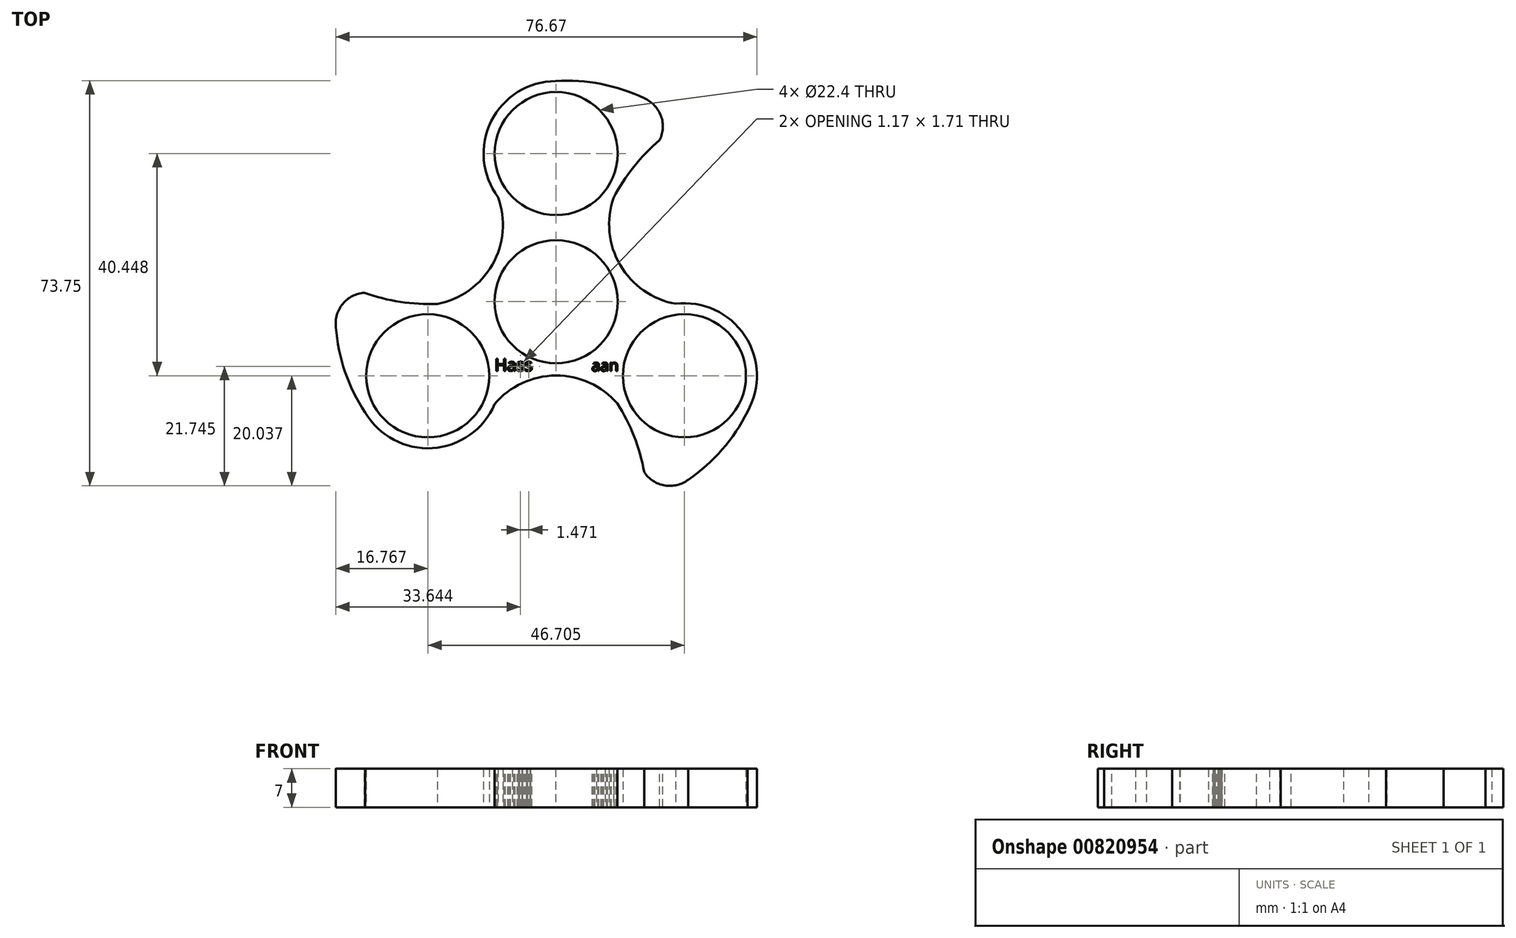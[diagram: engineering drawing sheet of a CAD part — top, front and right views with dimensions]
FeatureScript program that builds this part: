
annotation { "Feature Type Name" : "Feature", "Feature Type Description" : "" }
export const myFeature = defineFeature(function(context is Context, id is Id, definition is map)
    precondition{}
    {
        {
            var Q0;
            Q0=qCreatedBy(makeId("Top.planeOp"),FACE);
            var sketch = newSketch(context, id + "F0", { "sketchPlane" : qUnion([Q0])});
            skCircle(sketch, "E0", {"center": v(0, 0) * mm, "radius": 11.2 * mm});
            skArc(sketch, "E1", {"start": v(10.47, 18.92) * mm, "mid": v(11.4, 20.3) * mm, "end": v(12.14, 21.78) * mm});
            skCircle(sketch, "E2", {"center": v(0, 26.97) * mm, "radius": 11.2 * mm});
            skArc(sketch, "E3.1.0", {"start": v(-21.62, -0.4) * mm, "mid": v(-23.28, -0.28) * mm, "end": v(-24.93, -0.38) * mm});
            skCircle(sketch, "E3.1.1", {"center": v(-23.35, -13.48) * mm, "radius": 11.2 * mm});
            skArc(sketch, "E3.2.0", {"start": v(11.15, -18.52) * mm, "mid": v(11.88, -20.02) * mm, "end": v(12.8, -21.4) * mm});
            skCircle(sketch, "E3.2.1", {"center": v(23.35, -13.48) * mm, "radius": 11.2 * mm});
            skArc(sketch, "E4", {"start": v(10.47, 18.92) * mm, "mid": v(11.66, 6.67) * mm, "end": v(21.76, -0.38) * mm});
            skArc(sketch, "E5.1.0", {"start": v(-21.62, -0.4) * mm, "mid": v(-11.6, 6.77) * mm, "end": v(-10.55, 19.03) * mm});
            skArc(sketch, "E5.2.0", {"start": v(11.15, -18.52) * mm, "mid": v(-0.06, -13.43) * mm, "end": v(-11.2, -18.66) * mm});
            skArc(sketch, "E6", {"start": v(23.05, 32.47) * mm, "mid": v(12.24, 38.57) * mm, "end": v(-0.07, 40.17) * mm});
            skPoint(sketch, "E6.endSnap0", {"position": v(0.07, 40.17) * mm});
            skArc(sketch, "E7", {"start": v(23.05, 32.47) * mm, "mid": v(15.85, 26.54) * mm, "end": v(10.47, 18.92) * mm});
            skArc(sketch, "E8.1.0", {"start": v(-39.64, 3.72) * mm, "mid": v(-39.52, -8.69) * mm, "end": v(-34.75, -20.14) * mm});
            skArc(sketch, "E8.1.1", {"start": v(-39.64, 3.72) * mm, "mid": v(-30.9, 0.46) * mm, "end": v(-21.62, -0.4) * mm});
            skArc(sketch, "E8.2.0", {"start": v(16.6, -36.2) * mm, "mid": v(27.28, -29.88) * mm, "end": v(34.82, -20.02) * mm});
            skArc(sketch, "E8.2.1", {"start": v(16.6, -36.2) * mm, "mid": v(15.06, -27) * mm, "end": v(11.15, -18.52) * mm});
            skArc(sketch, "E9.trimOffspring", {"start": v(0.07, 40.17) * mm, "mid": v(-11.8, 32.9) * mm, "end": v(-10.55, 19.03) * mm});
            skArc(sketch, "E10.trimOffspring", {"start": v(-34.75, -20.14) * mm, "mid": v(-22.52, -26.66) * mm, "end": v(-11.2, -18.66) * mm});
            skArc(sketch, "E11.trimOffspring", {"start": v(34.82, -20.02) * mm, "mid": v(34.34, -6.17) * mm, "end": v(21.76, -0.38) * mm});
            skSolve(sketch);
        }
        {
            var Q0;
            Q0=makeQuery(id+"F0.imprint","IMPRINT",FACE,{"disambiguationData":[TD([[makeQuery(id+"F0.imprint","IMPRINT",EDGE,{"derivedFrom":sQuery(id+"F0.wireOp",EDGE,"E0")}),-1.0]])]});
            extrude(context, id + "F1", {"entities" : qUnion([Q0]), "depth" : 7 * mm, "offsetDistance" : 25 * mm});
        }
        {
            var Q0;
            Q0=makeQuery(id+"F1.opExtrude","CAP_FACE",FACE,{"disambiguationData":[OSD([sQuery(id+"F0.wireOp",EDGE,"E0"),sQuery(id+"F0.wireOp",EDGE,"E1"),sQuery(id+"F0.wireOp",EDGE,"E2"),sQuery(id+"F0.wireOp",EDGE,"E3.1.0"),sQuery(id+"F0.wireOp",EDGE,"E3.1.1"),sQuery(id+"F0.wireOp",EDGE,"E3.2.0"),sQuery(id+"F0.wireOp",EDGE,"E3.2.1"),sQuery(id+"F0.wireOp",EDGE,"E4"),sQuery(id+"F0.wireOp",EDGE,"E5.1.0"),sQuery(id+"F0.wireOp",EDGE,"E5.2.0")])],"isStart":false});
            var sketch = newSketch(context, id + "F2", { "sketchPlane" : qUnion([Q0])});
            skText(sketch, "E12", { "text": "Hass", "fontName": "OpenSans-Regular.ttf"});
            const initialGuessF2  = {"E12": [-0.01121, -0.0126, 1, 0, 0.00222]};
            skSetInitialGuess(sketch, initialGuessF2);
            skSolve(sketch);
        }
        {
            var Q0;
            Q0=qSketchRegion(id+"F2",true);
            extrude(context, id + "F3", {"entities" : qUnion([Q0]), "operationType" : NewBodyOperationType.REMOVE, "oppositeDirection" : true, "depth" : 13.4 * mm, "offsetDistance" : 25 * mm});
        }
        {
            var Q0;
            {var subQ0=sQuery(id+"F0.wireOp",EDGE,"E5.1.0");var subQ1=sQuery(id+"F0.wireOp",EDGE,"E4");var subQ2=sQuery(id+"F0.wireOp",EDGE,"E3.2.1");var subQ3=sQuery(id+"F0.wireOp",EDGE,"E3.2.0");var subQ4=sQuery(id+"F0.wireOp",EDGE,"E3.1.1");var subQ5=sQuery(id+"F0.wireOp",EDGE,"E5.2.0");var subQ6=sQuery(id+"F0.wireOp",EDGE,"E0");var subQ7=sQuery(id+"F0.wireOp",EDGE,"E3.1.0");var subQ8=sQuery(id+"F0.wireOp",EDGE,"E1");var subQ9=sQuery(id+"F0.wireOp",EDGE,"E2");Q0=makeQuery(id+"F3.boolean.opBoolean","SPLIT",FACE,{"disambiguationData":[TD([makeQuery(id+"F1.opExtrude","SWEPT_FACE",FACE,{"disambiguationData":[OSD([subQ6])]})])],"derivedFrom":makeQuery(id+"F1.opExtrude","CAP_FACE",FACE,{"disambiguationData":[OSD([subQ6,subQ8,subQ9,subQ7,subQ4,subQ3,subQ2,subQ1,subQ0,subQ5])],"isStart":false})});}
            var sketch = newSketch(context, id + "F4", { "sketchPlane" : qUnion([Q0])});
            skText(sketch, "E13", { "text": "aan", "fontName": "OpenSans-Regular.ttf"});
            const initialGuessF4  = {"E13": [0.00646, -0.01262, 1, 0, 0.00205]};
            skSetInitialGuess(sketch, initialGuessF4);
            skSolve(sketch);
        }
        {
            var Q0;
            Q0=qSketchRegion(id+"F4",true);
            extrude(context, id + "F5", {"entities" : qUnion([Q0]), "operationType" : NewBodyOperationType.REMOVE, "oppositeDirection" : true, "depth" : 9.9 * mm, "offsetDistance" : 25 * mm});
        }
        {
            var Q0;
            {var subQ43=sQuery(id+"F0.wireOp",EDGE,"E5.2.0");var subQ47=sQuery(id+"F0.wireOp",EDGE,"E5.1.0");var subQ51=sQuery(id+"F0.wireOp",EDGE,"E4");var subQ55=sQuery(id+"F0.wireOp",EDGE,"E3.2.1");var subQ59=sQuery(id+"F0.wireOp",EDGE,"E3.1.1");var subQ62=sQuery(id+"F0.wireOp",EDGE,"E2");var subQ66=sQuery(id+"F0.wireOp",EDGE,"E1");var subQ70=sQuery(id+"F0.wireOp",EDGE,"E3.1.0");var subQ75=sQuery(id+"F0.wireOp",EDGE,"E0");var subQ76=makeQuery(id+"F1.opExtrude","SWEPT_FACE",FACE,{"disambiguationData":[OSD([subQ75])]});var subQ79=sQuery(id+"F0.wireOp",EDGE,"E3.2.0");Q0=makeQuery(id+"F5.boolean.opBoolean","SPLIT",FACE,{"disambiguationData":[TD([subQ76])],"derivedFrom":makeQuery(id+"F3.boolean.opBoolean","SPLIT",FACE,{"disambiguationData":[TD([subQ76])],"derivedFrom":makeQuery(id+"F1.opExtrude","CAP_FACE",FACE,{"disambiguationData":[OSD([subQ75,subQ66,subQ62,subQ70,subQ59,subQ79,subQ55,subQ51,subQ47,subQ43])],"isStart":false})})});}
            var sketch = newSketch(context, id + "F6", { "sketchPlane" : qUnion([Q0])});
            skSolve(sketch);
        }
        {
            var Q0;
            Q0=makeQuery(id+"F6.imprint","IMPRINT",FACE,{"disambiguationData":[TD([[makeQuery(id+"F6.imprint","IMPRINT",EDGE,{"derivedFrom":makeQuery(id+"F1.opExtrude","CAP_EDGE",EDGE,{"disambiguationData":[OSD([sQuery(id+"F0.wireOp",EDGE,"E0")])],"isStart":false})}),-1.0]])]});
            var sketch = newSketch(context, id + "F7", { "sketchPlane" : qUnion([Q0])});
            skArc(sketch, "E14", {"start": v(-34.8, 1.62) * mm, "mid": v(-38.8, -0.36) * mm, "end": v(-40.08, -4.64) * mm});
            skArc(sketch, "E15", {"start": v(-34.8, 1.62) * mm, "mid": v(-44.08, 4.08) * mm, "end": v(-40.08, -4.64) * mm});
            skArc(sketch, "E16.1.0", {"start": v(16, -30.95) * mm, "mid": v(18.5, -40.21) * mm, "end": v(24.06, -32.39) * mm});
            skArc(sketch, "E16.1.1", {"start": v(16, -30.95) * mm, "mid": v(19.71, -33.43) * mm, "end": v(24.06, -32.39) * mm});
            skArc(sketch, "E16.2.0", {"start": v(18.8, 29.33) * mm, "mid": v(25.57, 36.13) * mm, "end": v(16.02, 37.03) * mm});
            skArc(sketch, "E16.2.1", {"start": v(18.8, 29.33) * mm, "mid": v(19.1, 33.79) * mm, "end": v(16.02, 37.03) * mm});
            skPoint(sketch, "E16.center", {"position": v(0, 0) * mm});
            skSolve(sketch);
        }
        {
            var Q0;
            Q0 = qSketchRegion(id + "F7", true);
            extrude(context, id + "F8", {"entities" : qUnion([Q0]), "operationType" : NewBodyOperationType.REMOVE, "oppositeDirection" : true, "depth" : 25 * mm, "offsetDistance" : 25 * mm});
        }
    });
